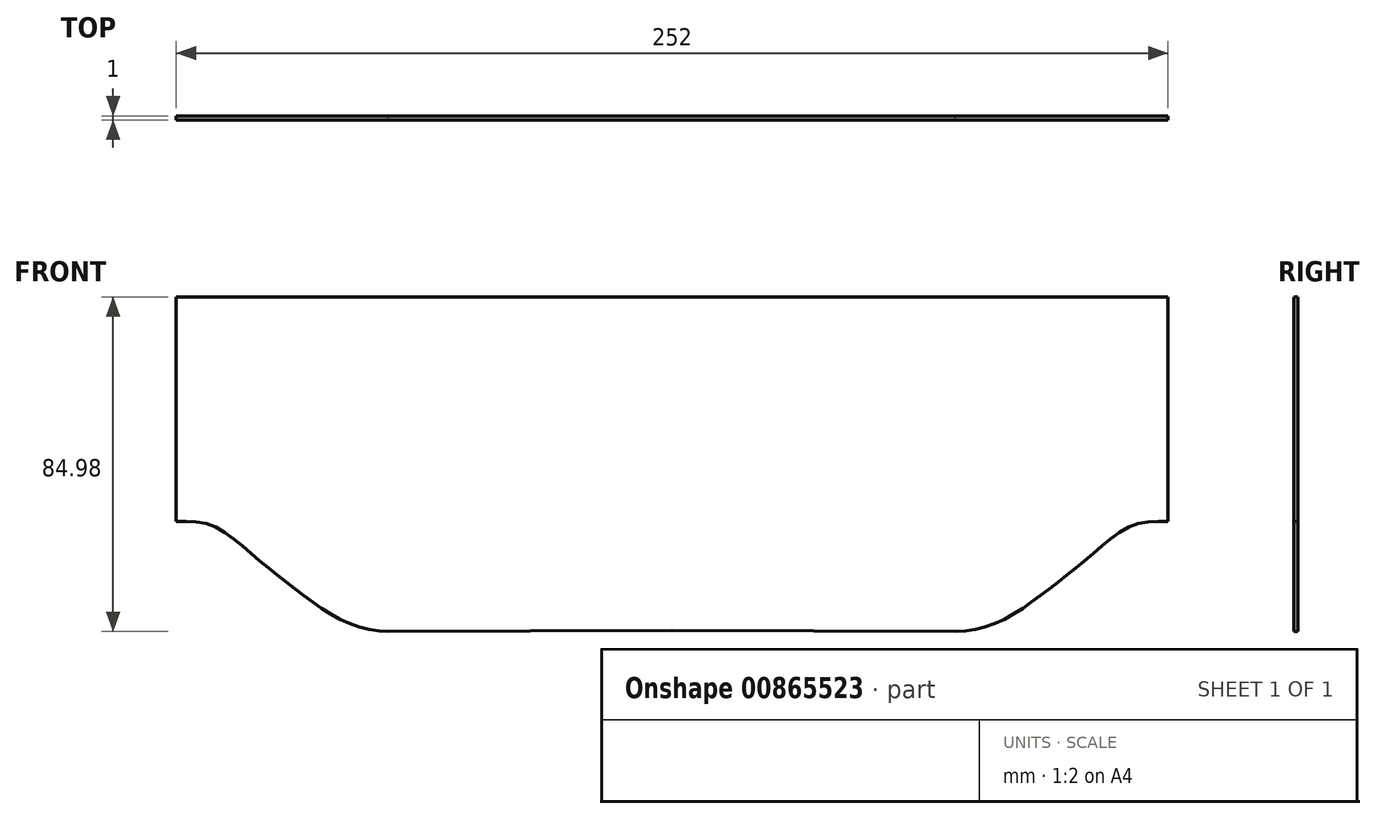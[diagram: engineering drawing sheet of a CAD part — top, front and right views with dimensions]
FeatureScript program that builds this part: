
annotation { "Feature Type Name" : "Feature", "Feature Type Description" : "" }
export const myFeature = defineFeature(function(context is Context, id is Id, definition is map)
    precondition{}
    {
        {
            var Q0;
            Q0=qCreatedBy(makeId("Front.planeOp"),FACE);
            var sketch = newSketch(context, id + "F0", { "sketchPlane" : qUnion([Q0])});
            skPoint(sketch, "E0", {"position": v(0, 28) * mm});
            skPoint(sketch, "E1", {"position": v(2, 28) * mm});
            skPoint(sketch, "E2", {"position": v(4, 27.97) * mm});
            skPoint(sketch, "E3", {"position": v(6, 27.79) * mm});
            skPoint(sketch, "E4", {"position": v(8, 27.35) * mm});
            skPoint(sketch, "E5", {"position": v(10, 26.56) * mm});
            skPoint(sketch, "E6", {"position": v(12, 25.41) * mm});
            skPoint(sketch, "E7", {"position": v(14, 24) * mm});
            skPoint(sketch, "E8", {"position": v(16, 22.41) * mm});
            skPoint(sketch, "E9", {"position": v(18, 20.71) * mm});
            skPoint(sketch, "E10", {"position": v(20, 19) * mm});
            skPoint(sketch, "E11", {"position": v(22, 17.33) * mm});
            skPoint(sketch, "E12", {"position": v(24, 15.7) * mm});
            skPoint(sketch, "E13", {"position": v(26, 14.11) * mm});
            skPoint(sketch, "E14", {"position": v(28, 12.55) * mm});
            skPoint(sketch, "E15", {"position": v(30, 11) * mm});
            skPoint(sketch, "E16", {"position": v(32, 9.47) * mm});
            skPoint(sketch, "E17", {"position": v(34, 7.97) * mm});
            skPoint(sketch, "E18", {"position": v(36, 6.54) * mm});
            skPoint(sketch, "E19", {"position": v(38, 5.21) * mm});
            skPoint(sketch, "E20", {"position": v(40, 4) * mm});
            skPoint(sketch, "E21", {"position": v(42, 2.95) * mm});
            skPoint(sketch, "E22", {"position": v(44, 2.05) * mm});
            skPoint(sketch, "E23", {"position": v(46, 1.32) * mm});
            skPoint(sketch, "E24", {"position": v(48, 0.74) * mm});
            skPoint(sketch, "E25", {"position": v(50, 0.33) * mm});
            skPoint(sketch, "E26", {"position": v(52, 0.08) * mm});
            skPoint(sketch, "E27", {"position": v(54, 0) * mm});
            skLineSegment(sketch, "E28", {"start": v(0, 28) * mm, "end": v(0, 84.98) * mm});
            skLineSegment(sketch, "E29", {"start": v(0, 84.98) * mm, "end": v(126, 84.98) * mm});
            skLineSegment(sketch, "E30", {"start": v(54, 0) * mm, "end": v(126, 0.29) * mm});
            skLineSegment(sketch, "E31", {"start": v(126, 84.98) * mm, "end": v(126, 0.29) * mm});
            skFitSpline(sketch, "E32", {"points": [v(0, 28) * mm, v(2, 28) * mm, v(4, 27.97) * mm, v(6, 27.79) * mm, v(8, 27.35) * mm, v(10, 26.56) * mm, v(12, 25.41) * mm, v(14, 24) * mm, v(16, 22.41) * mm, v(18, 20.71) * mm, v(20, 19) * mm, v(22, 17.33) * mm, v(24, 15.7) * mm, v(26, 14.11) * mm, v(28, 12.55) * mm, v(30, 11) * mm, v(32, 9.47) * mm, v(34, 7.97) * mm, v(36, 6.54) * mm, v(38, 5.21) * mm, v(40, 4) * mm, v(42, 2.95) * mm, v(44, 2.05) * mm, v(46, 1.32) * mm, v(48, 0.74) * mm, v(50, 0.33) * mm, v(52, 0.08) * mm, v(54, 0) * mm], "startDerivative": vector(58.03, 0.03) * mm, "endDerivative": vector(58.04, -1.26) * mm});
            skSolve(sketch);
        }
        {
            var Q0;
            Q0 = qSketchRegion(id + "F0", true);
            extrude(context, id + "F1", {"entities" : qUnion([Q0]), "depth" : 1 * mm, "offsetDistance" : 25 * mm});
        }
        {
            var Q0;
            Q0=makeQuery(id+"F1.opExtrude","SWEPT_BODY",BODY,{"disambiguationData":[OSD([sQuery(id+"F0.wireOp",EDGE,"E28"),sQuery(id+"F0.wireOp",EDGE,"E29"),sQuery(id+"F0.wireOp",EDGE,"E30"),sQuery(id+"F0.wireOp",EDGE,"E31"),sQuery(id+"F0.wireOp",EDGE,"E32")])]});
            var Q1;
            Q1=makeQuery(id+"F1.opExtrude","SWEPT_FACE",FACE,{"disambiguationData":[OSD([sQuery(id+"F0.wireOp",EDGE,"E31")])]});
            mirror(context, id + "F2", {"operationType" : NewBodyOperationType.ADD, "entities" : qUnion([Q0]), "mirrorPlane" : qUnion([Q1])});
        }
    });
